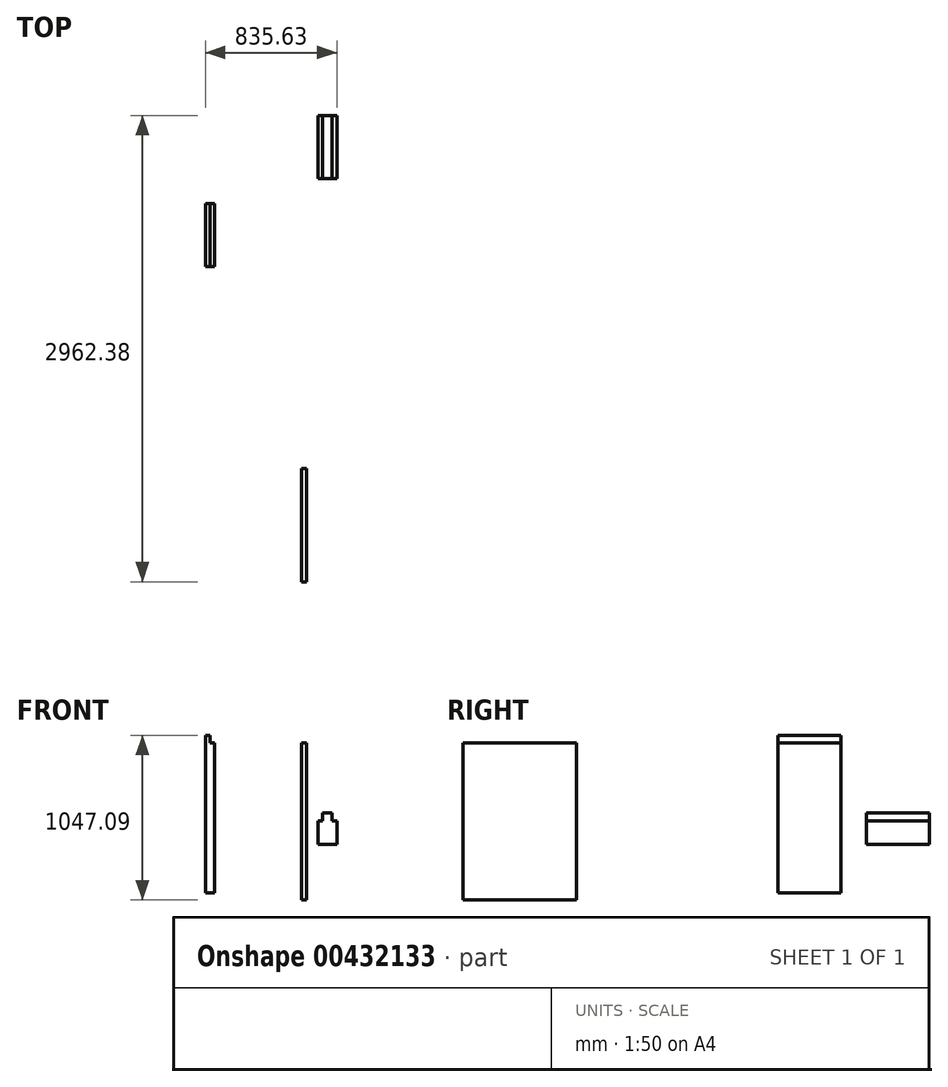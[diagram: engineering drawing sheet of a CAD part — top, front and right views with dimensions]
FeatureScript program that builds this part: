
annotation { "Feature Type Name" : "Feature", "Feature Type Description" : "" }
export const myFeature = defineFeature(function(context is Context, id is Id, definition is map)
    precondition{}
    {
        {
            var Q0;
            Q0=qCreatedBy(makeId("Right.planeOp"),FACE);
            var sketch = newSketch(context, id + "F0", { "sketchPlane" : qUnion([Q0])});
            skLineSegment(sketch, "E0.bottom", {"start": v(-160, 677.13) * mm, "end": v(240, 677.13) * mm});
            skLineSegment(sketch, "E0.top", {"start": v(-160, -322.87) * mm, "end": v(240, -322.87) * mm});
            skLineSegment(sketch, "E0.left", {"start": v(-160, 677.13) * mm, "end": v(-160, -322.87) * mm});
            skLineSegment(sketch, "E0.right", {"start": v(240, 677.13) * mm, "end": v(240, -322.87) * mm});
            skSolve(sketch);
        }
        {
            var Q0;
            Q0=makeQuery(id+"F0.imprint","IMPRINT",FACE,{"disambiguationData":[TD([[makeQuery(id+"F0.imprint","IMPRINT",EDGE,{"derivedFrom":sQuery(id+"F0.wireOp",EDGE,"E0.bottom")}),-1.0]])]});
            extrude(context, id + "F1", {"entities" : qUnion([Q0]), "depth" : 50 * mm});
        }
        {
            var Q0;
            Q0=makeQuery(id+"F1.opExtrude","SWEPT_FACE",FACE,{"disambiguationData":[OSD([sQuery(id+"F0.wireOp",EDGE,"E0.left")])]});
            var sketch = newSketch(context, id + "F2", { "sketchPlane" : qUnion([Q0])});
            skLineSegment(sketch, "E1.bottom", {"start": v(-612.18, 693.39) * mm, "end": v(-582.18, 693.39) * mm});
            skLineSegment(sketch, "E1.top", {"start": v(-612.18, -306.61) * mm, "end": v(-582.18, -306.61) * mm});
            skLineSegment(sketch, "E1.left", {"start": v(-612.18, 693.39) * mm, "end": v(-612.18, -306.61) * mm});
            skLineSegment(sketch, "E1.right", {"start": v(-582.18, 693.39) * mm, "end": v(-582.18, -306.61) * mm});
            skLineSegment(sketch, "E2.bottom", {"start": v(-582.18, 643.39) * mm, "end": v(-552.18, 643.39) * mm});
            skLineSegment(sketch, "E2.top", {"start": v(-582.18, -306.61) * mm, "end": v(-552.18, -306.61) * mm});
            skLineSegment(sketch, "E2.left", {"start": v(-582.18, 643.39) * mm, "end": v(-582.18, -306.61) * mm});
            skLineSegment(sketch, "E2.right", {"start": v(-552.18, 643.39) * mm, "end": v(-552.18, -306.61) * mm});
            skSolve(sketch);
        }
        {
            var Q0;
            Q0 = qSketchRegion(id + "F2", true);
            extrude(context, id + "F3", {"entities" : qUnion([Q0]), "depth" : 400 * mm});
        }
        {
            var Q0;
            Q0=makeQuery(id+"F1.opExtrude","SWEPT_BODY",BODY,{"disambiguationData":[OSD([sQuery(id+"F0.wireOp",EDGE,"E0.bottom"),sQuery(id+"F0.wireOp",EDGE,"E0.top"),sQuery(id+"F0.wireOp",EDGE,"E0.left"),sQuery(id+"F0.wireOp",EDGE,"E0.right")])]});
            deleteBodies(context, id + "F4", {"entities" : qUnion([Q0])});
        }
        {
            var Q0;
            Q0=qCreatedBy(makeId("Front.planeOp"),FACE);
            var sketch = newSketch(context, id + "F5", { "sketchPlane" : qUnion([Q0])});
            skLineSegment(sketch, "E3.bottom", {"start": v(133.45, 200) * mm, "end": v(193.45, 200) * mm});
            skLineSegment(sketch, "E3.top", {"start": v(133.45, 0) * mm, "end": v(193.45, 0) * mm});
            skLineSegment(sketch, "E3.left", {"start": v(133.45, 200) * mm, "end": v(133.45, 0) * mm});
            skLineSegment(sketch, "E3.right", {"start": v(193.45, 200) * mm, "end": v(193.45, 0) * mm});
            skLineSegment(sketch, "E4.bottom", {"start": v(193.45, 150) * mm, "end": v(223.45, 150) * mm});
            skLineSegment(sketch, "E4.top", {"start": v(193.45, 0) * mm, "end": v(223.45, 0) * mm});
            skLineSegment(sketch, "E4.left", {"start": v(193.45, 150) * mm, "end": v(193.45, 0) * mm});
            skLineSegment(sketch, "E4.right", {"start": v(223.45, 150) * mm, "end": v(223.45, 0) * mm});
            skLineSegment(sketch, "E5.bottom", {"start": v(133.45, 0) * mm, "end": v(103.45, 0) * mm});
            skLineSegment(sketch, "E5.top", {"start": v(133.45, 150) * mm, "end": v(103.45, 150) * mm});
            skLineSegment(sketch, "E5.left", {"start": v(133.45, 0) * mm, "end": v(133.45, 150) * mm});
            skLineSegment(sketch, "E5.right", {"start": v(103.45, 0) * mm, "end": v(103.45, 150) * mm});
            skSolve(sketch);
        }
        {
            var Q0;
            {var subQ0=sQuery(id+"F5.wireOp",EDGE,"E5.bottom");var subQ6=sQuery(id+"F5.wireOp",EDGE,"E3.bottom");var subQ9=sQuery(id+"F5.wireOp",EDGE,"E4.bottom");Q0=qUnion([makeQuery(id+"F5.imprint","IMPRINT",FACE,{"disambiguationData":[TD([[makeQuery(id+"F5.imprint","IMPRINT",EDGE,{"derivedFrom":subQ9}),-1.0]])]}),makeQuery(id+"F5.imprint","IMPRINT",FACE,{"disambiguationData":[TD([[makeQuery(id+"F5.imprint","IMPRINT",EDGE,{"derivedFrom":subQ6}),-1.0]])]}),makeQuery(id+"F5.imprint","IMPRINT",FACE,{"disambiguationData":[TD([[makeQuery(id+"F5.imprint","IMPRINT",EDGE,{"derivedFrom":subQ0}),-1.0]])]})]);}
            extrude(context, id + "F6", {"entities" : qUnion([Q0]), "oppositeDirection" : true, "depth" : 400 * mm});
        }
        {
            var Q0;
            Q0=makeQuery(id+"F0.imprint","IMPRINT",FACE,{"disambiguationData":[TD([[makeQuery(id+"F0.imprint","IMPRINT",EDGE,{"derivedFrom":sQuery(id+"F0.wireOp",EDGE,"E0.bottom")}),-1.0]])]});
            var sketch = newSketch(context, id + "F7", { "sketchPlane" : qUnion([Q0])});
            skLineSegment(sketch, "E6.bottom", {"start": v(-1842.38, 646.3) * mm, "end": v(-2562.38, 646.3) * mm});
            skLineSegment(sketch, "E6.top", {"start": v(-1842.38, -353.7) * mm, "end": v(-2562.38, -353.7) * mm});
            skLineSegment(sketch, "E6.left", {"start": v(-1842.38, 646.3) * mm, "end": v(-1842.38, -353.7) * mm});
            skLineSegment(sketch, "E6.right", {"start": v(-2562.38, 646.3) * mm, "end": v(-2562.38, -353.7) * mm});
            skSolve(sketch);
        }
        {
            var Q0;
            Q0=makeQuery(id+"F7.imprint","IMPRINT",FACE,{"disambiguationData":[TD([[makeQuery(id+"F7.imprint","IMPRINT",EDGE,{"derivedFrom":sQuery(id+"F7.wireOp",EDGE,"E6.bottom")}),1.0]])]});
            extrude(context, id + "F8", {"entities" : qUnion([Q0]), "depth" : 30 * mm});
        }
    });
